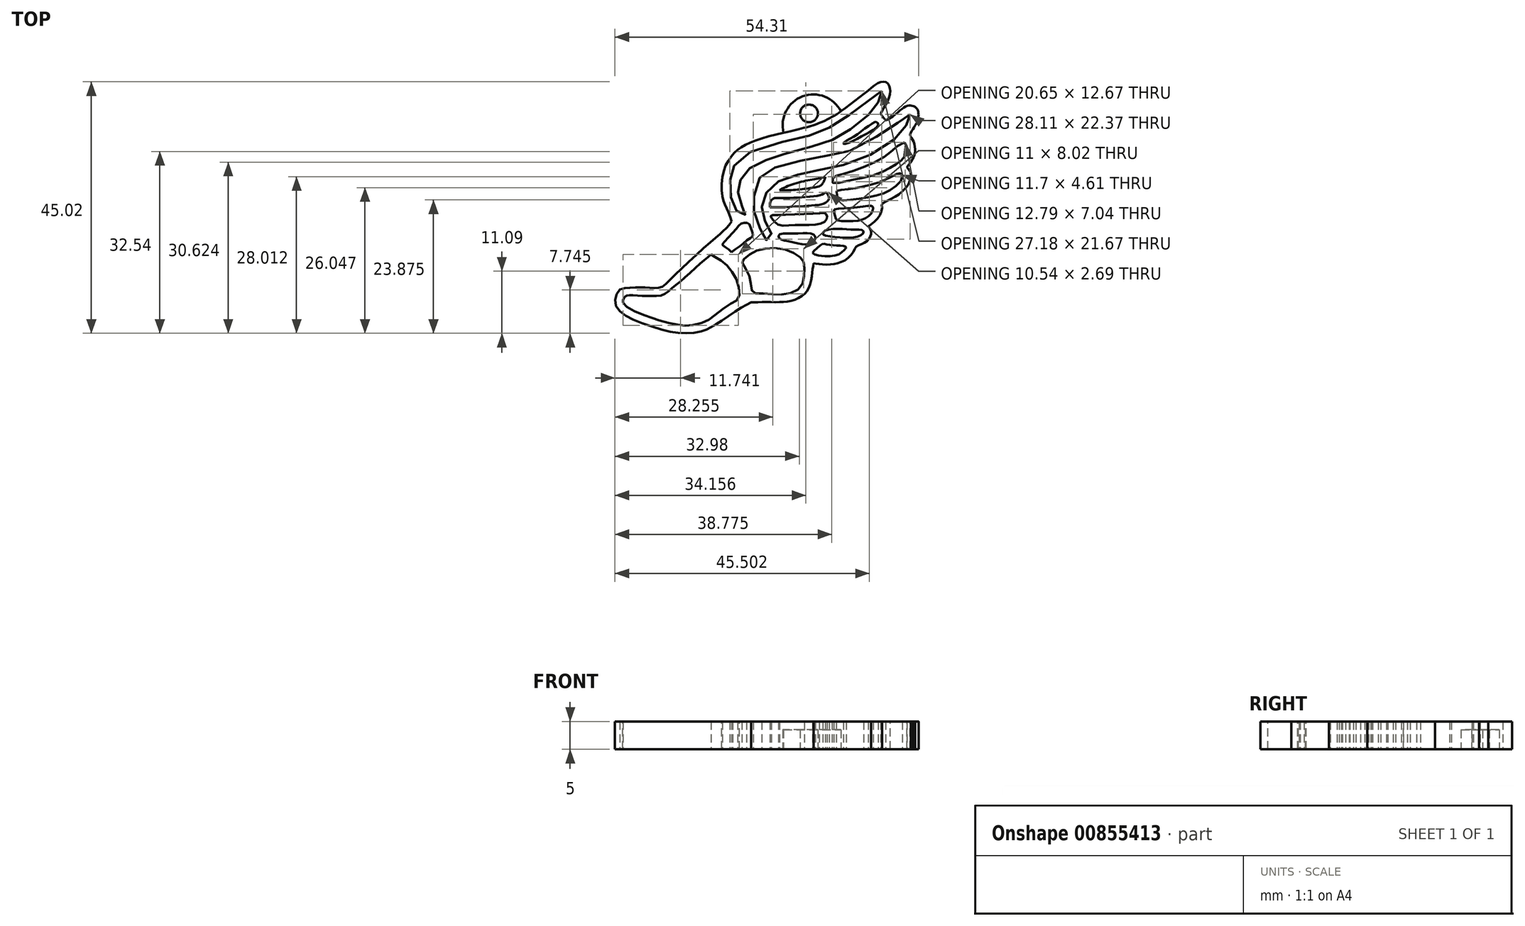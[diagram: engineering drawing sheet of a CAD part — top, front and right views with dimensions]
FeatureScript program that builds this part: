
annotation { "Feature Type Name" : "Feature", "Feature Type Description" : "" }
export const myFeature = defineFeature(function(context is Context, id is Id, definition is map)
    precondition{}
    {
        {
            var Q0;
            Q0=qCreatedBy(makeId("Top.planeOp"),FACE);
            var sketch = newSketch(context, id + "F0", { "sketchPlane" : qUnion([Q0])});
            skFitSpline(sketch, "E0", {"points": [v(-29.07, -18.82) * mm, v(-26.18, -18.42) * mm, v(-23.78, -18.5) * mm, v(-21.79, -18.44) * mm, v(-19.58, -16.56) * mm, v(-12.67, -10.2) * mm, v(-10.35, -8.14) * mm, v(-9.06, -6.63) * mm], "startDerivative": vector(18.36, 6.54) * mm, "endDerivative": vector(11.17, 13.94) * mm});
            skFitSpline(sketch, "E1", {"points": [v(-9.06, -6.63) * mm, v(-9.98, -4.24) * mm, v(-10.69, -2.35) * mm, v(-10.56, 2.14) * mm, v(-9.06, 5.12) * mm, v(-7.25, 6.73) * mm, v(-4.05, 8.14) * mm, v(2.02, 9.68) * mm, v(5.54, 10.6) * mm, v(8.95, 12.12) * mm, v(12.12, 14.33) * mm, v(15.26, 16.73) * mm, v(16.9, 18.02) * mm, v(18.02, 18.38) * mm, v(18.72, 18.2) * mm, v(19.15, 17.55) * mm, v(19.3, 16.77) * mm, v(18.98, 15.25) * mm, v(18.27, 13.9) * mm, v(17.61, 12.68) * mm], "startDerivative": vector(-17.03, 46.94) * mm, "endDerivative": vector(-15.8, -30.77) * mm});
            skFitSpline(sketch, "E2", {"points": [v(17.61, 12.68) * mm, v(17.96, 12.1) * mm, v(18.5, 11.47) * mm], "startDerivative": vector(0.68, -1.22) * mm, "endDerivative": vector(1.09, -1.2) * mm});
            skFitSpline(sketch, "E3", {"points": [v(18.5, 11.47) * mm, v(19.62, 12.08) * mm, v(20.98, 13.2) * mm, v(22.36, 14.08) * mm, v(23.16, 14.11) * mm, v(23.9, 13.77) * mm, v(24.27, 13.12) * mm, v(24.36, 12.51) * mm], "startDerivative": vector(7.13, 3.37) * mm, "endDerivative": vector(0.49, -5.41) * mm});
            skFitSpline(sketch, "E4", {"points": [v(24.36, 12.51) * mm, v(24.21, 11.47) * mm, v(23.58, 10.26) * mm, v(23.04, 9.4) * mm, v(22.83, 8.89) * mm, v(23.02, 8.44) * mm, v(23.45, 7.72) * mm, v(23.71, 6.33) * mm, v(23.66, 5.43) * mm, v(23.3, 4.63) * mm], "startDerivative": vector(-0.31, -8.68) * mm, "endDerivative": vector(-4, -7.28) * mm});
            skFitSpline(sketch, "E5", {"points": [v(23.3, 4.63) * mm, v(22.96, 3.98) * mm, v(22.43, 3.37) * mm, v(22.32, 3.05) * mm, v(22.53, 2.82) * mm, v(22.91, 2.12) * mm, v(22.98, 1.4) * mm, v(22.63, 0.14) * mm, v(21.97, -0.7) * mm, v(20.97, -1.67) * mm, v(20.03, -2.3) * mm, v(18.7, -2.97) * mm, v(18.02, -3.3) * mm, v(17.8, -3.53) * mm, v(17.8, -4.07) * mm, v(17.77, -4.73) * mm, v(17.35, -5.65) * mm, v(16.7, -6.46) * mm, v(15.74, -7.2) * mm, v(15.4, -7.5) * mm], "startDerivative": vector(-5.32, -13.35) * mm, "endDerivative": vector(-7.39, -6.89) * mm});
            skFitSpline(sketch, "E6", {"points": [v(15.4, -7.5) * mm, v(15.74, -7.99) * mm, v(15.89, -8.65) * mm, v(15.62, -9.48) * mm, v(14.9, -10.35) * mm, v(14.19, -10.65) * mm, v(13.5, -10.97) * mm, v(13.08, -11.3) * mm, v(12.78, -11.9) * mm, v(12.07, -12.88) * mm, v(11.13, -13.62) * mm, v(9.97, -14.07) * mm, v(9.02, -14.3) * mm, v(7.84, -14.35) * mm, v(6.76, -14.26) * mm, v(5.96, -14.18) * mm, v(5.6, -14.11) * mm], "startDerivative": vector(7.49, -8.62) * mm, "endDerivative": vector(-8.09, 1.63) * mm});
            skFitSpline(sketch, "E7", {"points": [v(5.6, -14.11) * mm, v(5.4, -15.2) * mm, v(5.2, -16.82) * mm, v(4.6, -18.78) * mm, v(3.72, -19.78) * mm, v(2.02, -20.72) * mm, v(0.32, -21.04) * mm, v(-1.78, -21.07) * mm, v(-4.06, -21.07) * mm, v(-5.62, -21.1) * mm], "startDerivative": vector(-2.4, -11.77) * mm, "endDerivative": vector(-13.99, -0.18) * mm});
            skFitSpline(sketch, "E8", {"points": [v(-5.62, -21.1) * mm, v(-6.68, -21.68) * mm, v(-8.52, -22.78) * mm, v(-10.94, -24.5) * mm, v(-12.45, -25.4) * mm, v(-13.64, -26) * mm, v(-15.22, -26.48) * mm, v(-18.05, -26.62) * mm, v(-20.93, -26.14) * mm, v(-25.33, -24.76) * mm, v(-28.42, -23.24) * mm, v(-29.8, -21.72) * mm, v(-29.8, -19.98) * mm, v(-29.07, -18.82) * mm], "startDerivative": vector(-17.52, -9.88) * mm, "endDerivative": vector(14.13, 17.38) * mm});
            skFitSpline(sketch, "E9", {"points": [v(17.8, 16.73) * mm, v(17.71, 15.92) * mm, v(16.6, 13.87) * mm, v(14.75, 11.82) * mm, v(10.32, 8.72) * mm, v(7.28, 7.37) * mm, v(0.26, 5.4) * mm, v(-3.05, 4.32) * mm, v(-5.89, 2.86) * mm, v(-7.29, 1.14) * mm, v(-7.9, -0.35) * mm, v(-7.9, -1.94) * mm, v(-7.26, -3.85) * mm, v(-6.43, -5.2) * mm, v(-6.61, -5.39) * mm, v(-7.64, -5.47) * mm, v(-8.37, -4.34) * mm, v(-9.2, -2.42) * mm, v(-9.34, 0.57) * mm, v(-8.93, 2.54) * mm, v(-7.18, 5.02) * mm, v(1.85, 8.07) * mm, v(7.2, 9.55) * mm, v(11.46, 12.09) * mm, v(15.77, 15.3) * mm, v(17.8, 16.73) * mm]});
            skFitSpline(sketch, "E10", {"points": [v(16.5, 11.15) * mm, v(14.89, 10.1) * mm, v(12.73, 8.53) * mm, v(11.1, 7.56) * mm, v(10.96, 7.28) * mm, v(11.86, 7.47) * mm, v(14.32, 8.69) * mm, v(16.5, 9.95) * mm, v(17.14, 10.8) * mm, v(16.74, 11.19) * mm, v(16.5, 11.15) * mm]});
            skFitSpline(sketch, "E11", {"points": [v(22.88, 12.56) * mm, v(22.88, 11.99) * mm, v(22.17, 10.63) * mm, v(20.84, 8.84) * mm, v(16.43, 5.67) * mm, v(10.4, 3.38) * mm, v(6.04, 2.49) * mm, v(2.68, 1.7) * mm, v(-0.56, 0.62) * mm, v(-2.3, -0.58) * mm, v(-3.35, -2.55) * mm, v(-3.67, -3.98) * mm, v(-3.57, -5.66) * mm, v(-2.75, -7.03) * mm, v(-2, -8.38) * mm, v(-2.07, -9.7) * mm, v(-2.3, -9.95) * mm, v(-3.12, -9.93) * mm, v(-3.5, -9.3) * mm, v(-4.6, -6.42) * mm, v(-5.14, -4.63) * mm, v(-5.23, -3.48) * mm, v(-4.68, -0.26) * mm, v(-3.67, 1.61) * mm, v(-1.2, 3.06) * mm, v(4.2, 4.43) * mm, v(9.6, 5.43) * mm, v(13.4, 6.59) * mm, v(19.73, 10.42) * mm, v(21.47, 11.62) * mm, v(22.88, 12.56) * mm]});
            skFitSpline(sketch, "E12", {"points": [v(21.81, 7.5) * mm, v(22.17, 6.97) * mm, v(22.29, 6.05) * mm, v(21.98, 5.22) * mm, v(21.4, 4.43) * mm, v(20.27, 3.56) * mm, v(18.66, 2.64) * mm, v(15.73, 1.5) * mm, v(12.58, 0.8) * mm, v(11, 0.49) * mm, v(9.07, 0.24) * mm, v(8.9, 0.8) * mm, v(9.26, 1.42) * mm, v(10.4, 1.78) * mm, v(14.24, 3.02) * mm, v(17.98, 4.78) * mm, v(19.9, 6.26) * mm, v(21.81, 7.5) * mm]});
            skFitSpline(sketch, "E13", {"points": [v(-0.5, -1.04) * mm, v(0.96, -0.3) * mm, v(3.7, 0.54) * mm, v(5.96, 0.98) * mm, v(7.7, 1.32) * mm], "startDerivative": vector(6, 3.41) * mm, "endDerivative": vector(7.42, 1.53) * mm});
            skFitSpline(sketch, "E14", {"points": [v(-0.5, -1.04) * mm, v(0.95, -1.04) * mm, v(4.47, -0.73) * mm, v(6.6, -0.33) * mm], "startDerivative": vector(4.71, -0.13) * mm, "endDerivative": vector(5.87, 1.3) * mm});
            skFitSpline(sketch, "E15", {"points": [v(6.6, -0.33) * mm, v(7.07, -0.01) * mm, v(7.55, 0.89) * mm, v(7.7, 1.32) * mm], "startDerivative": vector(1.58, 0.74) * mm, "endDerivative": vector(0.44, 1.37) * mm});
            skFitSpline(sketch, "E16", {"points": [v(-2.24, -4.1) * mm, v(-2.22, -3.3) * mm, v(-1.97, -2.83) * mm, v(-1.53, -2.49) * mm, v(0.13, -2.45) * mm, v(3.64, -2.3) * mm, v(6.82, -1.9) * mm, v(7.7, -1.42) * mm], "startDerivative": vector(-0.53, 8.02) * mm, "endDerivative": vector(5.93, 4.35) * mm});
            skFitSpline(sketch, "E17", {"points": [v(7.7, -1.42) * mm, v(8.12, -1.76) * mm, v(8.37, -2.53) * mm, v(8.1, -2.95) * mm, v(7.28, -3.5) * mm, v(5.5, -3.75) * mm, v(2, -4) * mm, v(-1.48, -4.11) * mm, v(-2.24, -4.1) * mm], "startDerivative": vector(5.57, -3.27) * mm, "endDerivative": vector(-6.55, 0.3) * mm});
            skFitSpline(sketch, "E18", {"points": [v(9.7, -1.17) * mm, v(9.85, -2.32) * mm, v(10.27, -2.83) * mm, v(11.66, -2.81) * mm, v(15.08, -2.34) * mm, v(17.9, -1.67) * mm, v(19.96, -0.54) * mm, v(21.37, 0.98) * mm, v(21.33, 1.8) * mm, v(21.03, 2.01) * mm, v(20.25, 1.76) * mm, v(18.19, 0.77) * mm, v(15.75, -0.05) * mm, v(13.2, -0.64) * mm, v(10.92, -0.94) * mm, v(9.7, -1.17) * mm]});
            skFitSpline(sketch, "E19", {"points": [v(-0.78, -7.23) * mm, v(-1.78, -6.23) * mm, v(-2.1, -5.71) * mm, v(-2.03, -5.57) * mm, v(-0.7, -5.46) * mm, v(4.35, -5.3) * mm, v(7.32, -5.1) * mm, v(7.6, -5.1) * mm, v(7.89, -5.4) * mm, v(7.98, -5.91) * mm, v(7.68, -6.53) * mm, v(6.7, -7.07) * mm, v(4.05, -7.28) * mm, v(1.1, -7.3) * mm, v(-0.78, -7.23) * mm]});
            skFitSpline(sketch, "E20", {"points": [v(9.22, -4.85) * mm, v(9.56, -6.07) * mm, v(9.8, -6.4) * mm, v(11.66, -6.57) * mm, v(13.85, -6.44) * mm, v(14.94, -6.03) * mm, v(15.87, -5.23) * mm, v(16.17, -4.5) * mm, v(16.23, -4.05) * mm, v(16.07, -3.92) * mm, v(15.85, -3.83) * mm, v(14.62, -3.94) * mm, v(11.45, -4.24) * mm, v(9.36, -4.49) * mm, v(9.22, -4.85) * mm]});
            skFitSpline(sketch, "E21", {"points": [v(-0.44, -8.93) * mm, v(-0.69, -9.27) * mm, v(-0.44, -9.75) * mm, v(0.4, -10.04) * mm, v(2.3, -10.47) * mm, v(3.92, -10.72) * mm, v(5.14, -10.65) * mm, v(5.66, -10.13) * mm, v(5.91, -9.54) * mm, v(5.7, -9.07) * mm, v(5.05, -8.8) * mm, v(3.53, -8.75) * mm, v(1.13, -8.77) * mm, v(-0.44, -8.93) * mm]});
            skFitSpline(sketch, "E22", {"points": [v(7.61, -8.27) * mm, v(7.25, -8.64) * mm, v(7.32, -9) * mm, v(8.39, -9.25) * mm, v(10.43, -9.52) * mm, v(12.22, -9.52) * mm, v(13.53, -9.32) * mm, v(14.33, -8.9) * mm, v(14.53, -8.5) * mm, v(14.35, -8.23) * mm, v(13.74, -8.1) * mm, v(12.3, -8.07) * mm, v(10.86, -7.98) * mm, v(9.07, -7.98) * mm, v(7.61, -8.27) * mm]});
            skFitSpline(sketch, "E23", {"points": [v(5.4, -12.31) * mm, v(6.33, -12.69) * mm, v(7.38, -12.86) * mm, v(9.68, -12.67) * mm, v(10.78, -12.01) * mm, v(11.4, -11.38) * mm, v(11.33, -11.15) * mm, v(10.74, -11) * mm, v(9.43, -10.92) * mm, v(8.3, -10.81) * mm, v(7.52, -10.63) * mm, v(7.1, -10.7) * mm, v(6.17, -11.46) * mm, v(5.4, -12.31) * mm]});
            skFitSpline(sketch, "E24", {"points": [v(-9.1, -12.16) * mm, v(-9.63, -11.62) * mm, v(-10.22, -11.22) * mm, v(-10.68, -10.85) * mm, v(-10.7, -10.76) * mm, v(-10.67, -10.62) * mm, v(-10.5, -10.42) * mm, v(-9.6, -9.4) * mm, v(-8.42, -8.13) * mm, v(-7.82, -7.41) * mm, v(-7.4, -7.06) * mm, v(-7.01, -6.9) * mm, v(-6.62, -6.87) * mm, v(-6.14, -6.96) * mm, v(-5.87, -7.16) * mm, v(-5.6, -7.91) * mm, v(-5.35, -8.63) * mm, v(-5.25, -8.98) * mm, v(-5.23, -9.2) * mm, v(-5.45, -9.42) * mm, v(-5.73, -9.61) * mm, v(-6.57, -10.2) * mm, v(-7.4, -10.88) * mm, v(-8.37, -11.6) * mm, v(-8.87, -11.95) * mm], "startDerivative": vector(-10.75, 12.22) * mm, "endDerivative": vector(-10.51, -7.43) * mm});
            skFitSpline(sketch, "E25", {"points": [v(-8.87, -11.95) * mm, v(-9.1, -12.16) * mm], "startDerivative": vector(-0.23, -0.22) * mm, "endDerivative": vector(-0.23, -0.22) * mm});
            skFitSpline(sketch, "E26", {"points": [v(-28.53, -21.16) * mm, v(-27.44, -22.15) * mm, v(-24.1, -23.63) * mm, v(-22, -24.33) * mm, v(-18.72, -25.13) * mm, v(-16.6, -25.23) * mm, v(-13.81, -24.59) * mm, v(-11.98, -23.34) * mm, v(-9.1, -21.29) * mm, v(-7.88, -20.52) * mm, v(-7.81, -18.27) * mm, v(-8.87, -15.83) * mm, v(-10.5, -13.97) * mm, v(-12.08, -12.98) * mm, v(-12.75, -12.56) * mm], "startDerivative": vector(14.53, -17.09) * mm, "endDerivative": vector(-14.15, 9.16) * mm});
            skFitSpline(sketch, "E27", {"points": [v(-12.75, -12.56) * mm, v(-13.71, -13.32) * mm, v(-15.37, -14.75) * mm, v(-17.85, -17) * mm, v(-19.38, -18.27) * mm, v(-20.58, -19.29) * mm, v(-21.68, -19.9) * mm, v(-23.13, -19.95) * mm, v(-24.62, -19.97) * mm, v(-26.1, -19.9) * mm, v(-27.21, -19.82) * mm, v(-27.7, -19.86) * mm, v(-28.17, -20.09) * mm, v(-28.55, -20.8) * mm, v(-28.53, -21.16) * mm], "startDerivative": vector(-13.08, -10.1) * mm, "endDerivative": vector(1.75, -8.49) * mm});
            skFitSpline(sketch, "E28", {"points": [v(-7.2, -13.97) * mm, v(-6.33, -15.5) * mm, v(-5.79, -16.98) * mm, v(-5.54, -18.64) * mm, v(-5.27, -19.39) * mm, v(-4.06, -19.52) * mm, v(-1.7, -19.68) * mm, v(0.86, -19.57) * mm, v(2.7, -18.86) * mm, v(3.7, -17.5) * mm, v(3.9, -15.8) * mm, v(3.88, -14.28) * mm, v(3.54, -13.42) * mm, v(2.51, -12.56) * mm, v(0.38, -11.6) * mm, v(-2.68, -11.45) * mm, v(-4.77, -11.95) * mm, v(-6.33, -12.9) * mm, v(-7.17, -13.65) * mm, v(-7.2, -13.97) * mm]});
            skArc(sketch, "E29", {"start": v(10.45, 13.1) * mm, "mid": v(3.62, 15.76) * mm, "end": v(0.21, 9.26) * mm});
            skCircle(sketch, "E30", {"center": v(4.76, 12.71) * mm, "radius": 1.59 * mm});
            skSolve(sketch);
        }
        {
            var Q0;
            {var subQ5=sQuery(id+"F0.wireOp",EDGE,"E0");Q0=makeQuery(id+"F0.imprint","IMPRINT",FACE,{"disambiguationData":[TD([[makeQuery(id+"F0.imprint","IMPRINT",EDGE,{"derivedFrom":subQ5}),-1.0]])]});}
            extrude(context, id + "F1", {"entities" : qUnion([Q0]), "depth" : 5 * mm, "offsetDistance" : 25 * mm});
        }
        {
            var Q0;
            {var subQ0=sQuery(id+"F0.wireOp",EDGE,"E29");Q0=makeQuery(id+"F0.imprint","IMPRINT",FACE,{"disambiguationData":[TD([[makeQuery(id+"F0.imprint","IMPRINT",EDGE,{"derivedFrom":subQ0}),1.0]])]});}
            extrude(context, id + "F2", {"entities" : qUnion([Q0]), "operationType" : NewBodyOperationType.ADD, "depth" : 3.5 * mm, "offsetDistance" : 25 * mm});
        }
    });
